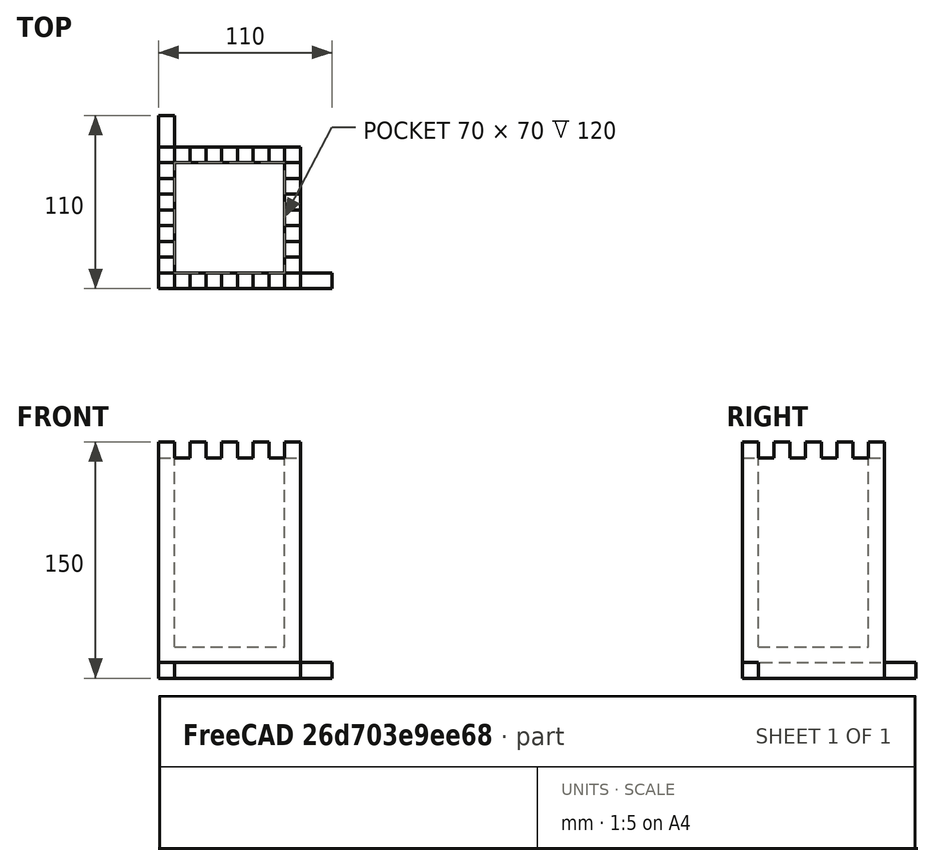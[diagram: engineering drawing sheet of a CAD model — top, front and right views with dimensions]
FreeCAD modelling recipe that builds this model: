
FCSTD DOCUMENT  (FreeCAD 1.0R39319 (Git))
Label: ojt1_t10r02_tower
License: All rights reserved
LicenseURL: https://en.wikipedia.org/wiki/All_rights_reserved
objects: Part::Box×4, Part::FeaturePython×2, Part::Cut×2, Part::MultiFuse×1
note: 7 computed .brp shape members not serialized (recipe doc carries the construction recipe); baked Part::Feature solids carry a one-line shape summary decoded from their .brp

FEATURE [Part::Box] Box  label="Cub"
  AttacherType = Attacher::AttachEngine3D
  Height = 10
  Length = 110
  Width = 10
FEATURE [Part::FeaturePython] Array  # Draft array (typed FeaturePython)
  AlwaysSyncPlacement = false
  Angle = 360
  ArrayType = 0
  Axis = (0,0,1)
  Base = -> Box
  Center = (0,0,0)
  Count = 4
  ExpandArray = false
  Fuse = false
  IntervalAxis = (0,0,0)
  IntervalX = (100,0,0)
  IntervalY = (0,20,0)
  IntervalZ = (0,0,100)
  NumberCircles = 3
  NumberPolar = 5
  NumberX = 1
  NumberY = 4
  NumberZ = 1
  PlacementList = 4 placements: arithmetic series from (0,0,0) step (0,20,0) to (0,60,0)
  RadialDistance = 50
  ScaleList = (4) [(1,1,1),(1,1,1),(1,1,1),(1,1,1)]
  Symmetry = 1
  TangentialDistance = 25
FEATURE [Part::Box] Box001  label="Cub001"
  AttacherType = Attacher::AttachEngine3D
  Height = 10
  Length = 10
  Width = 110
FEATURE [Part::FeaturePython] Array001  # Draft array (typed FeaturePython)
  AlwaysSyncPlacement = false
  Angle = 360
  ArrayType = 0
  Axis = (0,0,1)
  Base = -> Box001
  Center = (0,0,0)
  Count = 4
  ExpandArray = false
  Fuse = false
  IntervalAxis = (0,0,0)
  IntervalX = (20,0,0)
  IntervalY = (0,100,0)
  IntervalZ = (0,0,100)
  NumberCircles = 3
  NumberPolar = 5
  NumberX = 4
  NumberY = 1
  NumberZ = 1
  Placement = pos=(20,-20,0) rot=(0,0,1;0rad)
  PlacementList = 4 placements: arithmetic series from (0,0,0) step (20,0,0) to (60,0,0)
  RadialDistance = 50
  ScaleList = (4) [(1,1,1),(1,1,1),(1,1,1),(1,1,1)]
  Symmetry = 1
  TangentialDistance = 25
FEATURE [Part::MultiFuse] Fusion
  Placement = pos=(-10,10,140) rot=(0,0,1;0rad)
  Shapes = -> [Array,Array001]
FEATURE [Part::Box] Box002  label="Cub002"
  AttacherType = Attacher::AttachEngine3D
  Height = 150
  Length = 90
  Width = 90
FEATURE [Part::Box] Box003  label="Cub003"
  AttacherType = Attacher::AttachEngine3D
  Height = 130
  Length = 70
  Placement = pos=(10,10,20) rot=(0,0,1;0rad)
  Width = 70
FEATURE [Part::Cut] Cut
  Base = -> Box002
  Tool = -> Box003
FEATURE [Part::Cut] Cut001
  Base = -> Cut
  Tool = -> Fusion
